FCSTD DOCUMENT  (FreeCAD 0.20R29603 (Git))
Label: UNO FootPrint
License: All rights reserved
LicenseURL: http://en.wikipedia.org/wiki/All_rights_reserved
objects: Sketcher::SketchObject×1, PartDesign::Body×1, App::Part×1
note: 2 computed .brp shape members not serialized (recipe doc carries the construction recipe); baked Part::Feature solids carry a one-line shape summary decoded from their .brp

FEATURE [Sketcher::SketchObject] Sketch002
  FullyConstrained = false
  MapMode = 5
  Placement = pos=(0,0,0) rot=(1,0,0;3.14159rad)
  sketch-geometry (12):
    g0: LineSegment StartX=-26.75 StartY=33 StartZ=0 EndX=-26.75 EndY=-33 EndZ=0
    g1: LineSegment StartX=-26.75 StartY=-33 StartZ=0 EndX=26.75 EndY=-33 EndZ=0
    g2: LineSegment StartX=26.75 StartY=-33 StartZ=0 EndX=26.75 EndY=33 EndZ=0
    g3: LineSegment StartX=26.75 StartY=33 StartZ=0 EndX=13.25 EndY=33 EndZ=0
    g4: LineSegment StartX=13.25 StartY=33 StartZ=0 EndX=10.75 EndY=35.5 EndZ=0
    g5: LineSegment StartX=10.75 StartY=35.5 StartZ=0 EndX=-21.75 EndY=35.5 EndZ=0
    g6: LineSegment StartX=-21.75 StartY=35.5 StartZ=0 EndX=-24.25 EndY=33 EndZ=0
    g7: LineSegment StartX=-24.25 StartY=33 StartZ=0 EndX=-26.75 EndY=33 EndZ=0
    g8: Circle CenterX=-19.15 CenterY=33 CenterZ=0 NormalX=0 NormalY=0 NormalZ=1 AngleXU=0 Radius=1.75
    g9: Circle CenterX=8.15 CenterY=33 CenterZ=0 NormalX=0 NormalY=0 NormalZ=1 AngleXU=0 Radius=1.75
    g10: Circle CenterX=24.25 CenterY=-17.8 CenterZ=0 NormalX=0 NormalY=0 NormalZ=1 AngleXU=0 Radius=1.75
    g11: Circle CenterX=-24.25 CenterY=-19 CenterZ=0 NormalX=0 NormalY=0 NormalZ=1 AngleXU=0 Radius=1.75
  constraints (11):
    c: DistanceX(g8,g9) = 27.3
    c: DistanceX(g11,g10) = 48.5
    c: DistanceX(g11,g8) = 5.1
    c: DistanceY(g11,g10) = 1.2
    c: DistanceY(g9,g8) = 0
    c: DistanceY(g10,g9) = 50.8
    c: DistanceY(g0,g5) = 68.5
    c: DistanceX(g0,g1) = 53.5
    c: DistanceY(g8,g5) = 2.5
    c: DistanceY(g9,g4) = 2.5
    c: DistanceX(g10,g1) = 2.5
FEATURE [PartDesign::Body] Body
  Group = -> [Sketch002]
  Origin = -> Origin001
FEATURE [App::Part] Part
  Group = -> [Body]
  Origin = -> Origin
